# Revit family: Shower-Floor_Drain-KOHLER-Stripe-K-33503T-1
name_source: partatom
category: Plumbing Fixtures
units: mm (PartAtom-declared; Revit-internal decimal feet)

## family parameters
Cut with Voids When Loaded = No
Host = Face
Maintain Annotation Orientation = No
OmniClass Number = 23.39.29.11
OmniClass Title = Waste Water Drains
Part Type = Normal
Room Calculation Point = No
Round Connector Dimension = Use Diameter
Shared = No

## types (2) — shared parameters
ADA Compliant = No
Assembly Code = D2030300
CW Connection = No
Cold Water Inlet = Cold Water Inlet
Date Modified = 07/10/2025
Default Elevation = 0"
Description = Kitchen and bathroom floor drain (stripe)
Flow Rate = 0 GPM
HW Connection = No
Height = 2 1/8"
Hot Water Inlet = Hot Water Inlet
Length = 3 15/16"
Manufacturer = Kohler Co.
Master Format 2014 = 22 13 19.13
Master Format 2014 Name = Sanitary Drains
Material = Plastic Construction
Pressure = 0.00 psi
Product Name = Stripe
URL = http://www.kohler.com.cn
Vent Connection = No
Waste Connection = Yes
Waste Water Outlet = Waste Water Outlet
WaterSense Certified = No
Width = 3 15/16"

## per-type parameters (varying)
| type | Finish | Model | Product Documentation Link | Product Page URL | Type |
| CP-Polished Chrome | Kohler-Plastic-CP-Polished_Chrome | K-33503T-CP | https://files.kohler.com.cn | https://www.kohler.com.cn | 1 |
| LBN-Non Pvd Brushed Nickel | KOHLER-Plastic-LBN-Non_Pvd_Brushed_Nickel | K-33503T-LBN |  |  | 2 |

## geometry (parser evidence)
native form markers: Sweep x6
no freeform markers — native parametric forms only
